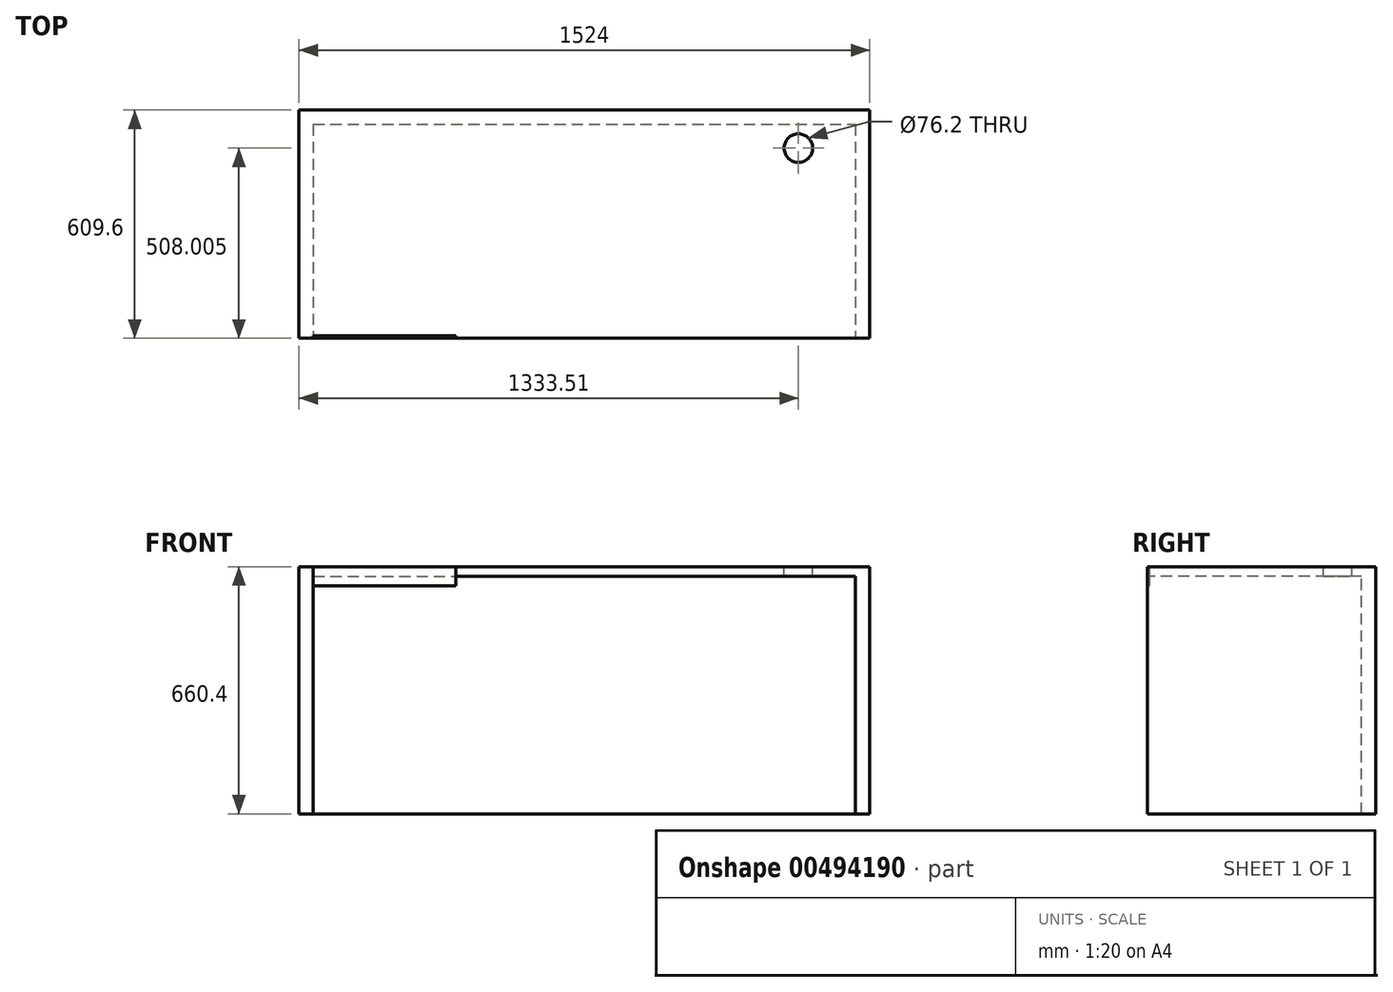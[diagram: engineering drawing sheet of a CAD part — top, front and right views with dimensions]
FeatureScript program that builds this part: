
annotation { "Feature Type Name" : "Feature", "Feature Type Description" : "" }
export const myFeature = defineFeature(function(context is Context, id is Id, definition is map)
    precondition{}
    {
        {
            var Q0;
            Q0=qCreatedBy(makeId("Top.planeOp"),FACE);
            var sketch = newSketch(context, id + "F0", { "sketchPlane" : qUnion([Q0])});
            skLineSegment(sketch, "E0.bottom", {"start": v(-763.73, 338.12) * mm, "end": v(760.27, 338.12) * mm});
            skLineSegment(sketch, "E0.top", {"start": v(-763.73, -271.48) * mm, "end": v(760.27, -271.48) * mm});
            skLineSegment(sketch, "E0.left", {"start": v(-763.73, 338.12) * mm, "end": v(-763.73, -271.48) * mm});
            skLineSegment(sketch, "E0.right", {"start": v(760.27, 338.12) * mm, "end": v(760.27, -271.48) * mm});
            skLineSegment(sketch, "E1", {"start": v(722.17, 338.12) * mm, "end": v(722.17, -271.48) * mm});
            skLineSegment(sketch, "E2", {"start": v(-725.63, 338.12) * mm, "end": v(-725.63, -271.48) * mm});
            skCircle(sketch, "E3", {"center": v(569.77, 236.52) * mm, "radius": 38.1 * mm});
            skLineSegment(sketch, "E4", {"start": v(569.77, 236.52) * mm, "end": v(722.17, 236.52) * mm});
            skLineSegment(sketch, "E5", {"start": v(569.77, 236.52) * mm, "end": v(569.77, 338.12) * mm});
            skLineSegment(sketch, "E6", {"start": v(-725.63, 300.02) * mm, "end": v(722.17, 300.02) * mm});
            skLineSegment(sketch, "E7.bottom", {"start": v(-725.63, -265.13) * mm, "end": v(-344.63, -265.13) * mm});
            skLineSegment(sketch, "E7.top", {"start": v(-725.63, -271.48) * mm, "end": v(-344.63, -271.48) * mm});
            skLineSegment(sketch, "E7.left", {"start": v(-725.63, -265.13) * mm, "end": v(-725.63, -271.48) * mm});
            skLineSegment(sketch, "E7.right", {"start": v(-344.63, -265.13) * mm, "end": v(-344.63, -271.48) * mm});
            skSolve(sketch);
        }
        {
            var Q0;
            {var subQ0=sQuery(id+"F0.wireOp",EDGE,"E4");var subQ1=sQuery(id+"F0.wireOp",EDGE,"E1");var subQ2=makeQuery(id+"F0.imprint","INTERSECT",VERTEX,{"derivedFrom":[subQ1,subQ0]});Q0=makeQuery(id+"F0.imprint","IMPRINT",FACE,{"disambiguationData":[TD([[makeQuery(id+"F0.imprint","IMPRINT",EDGE,{"disambiguationData":[TD([[subQ2,1.0]])],"derivedFrom":subQ1}),-1.0]])]});}
            var Q1;
            {var subQ1=sQuery(id+"F0.wireOp",EDGE,"E0.top");var subQ5=sQuery(id+"F0.wireOp",EDGE,"E1");var subQ6=makeQuery(id+"F0.imprint","INTERSECT",VERTEX,{"derivedFrom":[subQ1,subQ5]});Q1=makeQuery(id+"F0.imprint","IMPRINT",FACE,{"disambiguationData":[TD([[makeQuery(id+"F0.imprint","IMPRINT",EDGE,{"disambiguationData":[TD([[subQ6,1.0]])],"derivedFrom":subQ1}),1.0]])]});}
            extrude(context, id + "F1", {"entities" : qUnion([Q0, Q1]), "oppositeDirection" : true, "depth" : 25.4 * mm});
        }
        {
            var Q0;
            {var subQ0=sQuery(id+"F0.wireOp",EDGE,"E2");var subQ1=sQuery(id+"F0.wireOp",EDGE,"E0.bottom");var subQ2=makeQuery(id+"F0.imprint","INTERSECT",VERTEX,{"derivedFrom":[subQ1,subQ0]});Q0=makeQuery(id+"F0.imprint","IMPRINT",FACE,{"disambiguationData":[TD([[makeQuery(id+"F0.imprint","IMPRINT",EDGE,{"disambiguationData":[TD([[subQ2,-1.0]])],"derivedFrom":subQ1}),-1.0]])]});}
            var Q1;
            {var subQ0=sQuery(id+"F0.wireOp",EDGE,"E1");var subQ1=sQuery(id+"F0.wireOp",EDGE,"E0.bottom");var subQ2=makeQuery(id+"F0.imprint","INTERSECT",VERTEX,{"derivedFrom":[subQ1,subQ0]});Q1=makeQuery(id+"F0.imprint","IMPRINT",FACE,{"disambiguationData":[TD([[makeQuery(id+"F0.imprint","IMPRINT",EDGE,{"disambiguationData":[TD([[subQ2,1.0]])],"derivedFrom":subQ1}),-1.0]])]});}
            var Q2;
            {var subQ4=sQuery(id+"F0.wireOp",EDGE,"E0.right");Q2=makeQuery(id+"F0.imprint","IMPRINT",FACE,{"disambiguationData":[TD([[makeQuery(id+"F0.imprint","IMPRINT",EDGE,{"derivedFrom":subQ4}),-1.0]])]});}
            var Q3;
            {var subQ4=sQuery(id+"F0.wireOp",EDGE,"E0.left");Q3=makeQuery(id+"F0.imprint","IMPRINT",FACE,{"disambiguationData":[TD([[makeQuery(id+"F0.imprint","IMPRINT",EDGE,{"derivedFrom":subQ4}),1.0]])]});}
            extrude(context, id + "F2", {"entities" : qUnion([Q0, Q1, Q2, Q3]), "operationType" : NewBodyOperationType.ADD, "oppositeDirection" : true, "depth" : 660.4 * mm});
        }
        {
            var Q0;
            Q0=makeQuery(id+"F0.imprint","IMPRINT",FACE,{"disambiguationData":[TD([[makeQuery(id+"F0.imprint","IMPRINT",EDGE,{"derivedFrom":sQuery(id+"F0.wireOp",EDGE,"E7.bottom")}),-1.0]])]});
            var Q1;
            Q1=sQuery(id+"F0.wireOp",EDGE,"E7.bottom");
            extrude(context, id + "F3", {"entities" : qUnion([Q0]), "surfaceEntities" : qUnion([Q1]), "oppositeDirection" : true, "depth" : 50.8 * mm});
        }
    });
